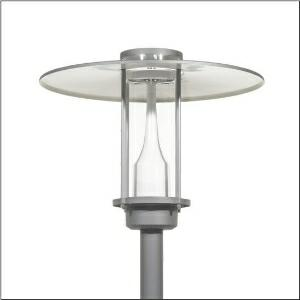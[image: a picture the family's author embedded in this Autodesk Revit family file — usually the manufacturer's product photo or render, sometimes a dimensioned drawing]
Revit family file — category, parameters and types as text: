
# Revit family: city-light_plus_iq___p1_0a_5xa5275ff14h_c9da
name_source: partatom
category: Lighting Fixtures
units: mm (PartAtom-declared; Revit-internal decimal feet)

## family parameters
Cut with Voids When Loaded = No
Host = Face
Light Source = No
Part Type = Normal
Room Calculation Point = No
Round Connector Dimension = Use Diameter
Shared = No

## types (1)
- --- (1 x LED, 1440 lm, 10.5 W, 3000K)
    Apparent Load = 11 VA
    CIE Flux Codes = 32 61 90 96 100
    Color Rendering = 70
    Color Temperature = 3000K
    Default Elevation = 1800 mm
    Description = City-Light Plus iQ, mast luminaire, Module 540 iQ-SR, primary light control with 3 zone facetted reflector, of plastic, silver coated, highly specular, structured, primary optical cover: cover, of PMMA, transparent, light distribution: P1.0a, light emission: direct distribution, primary light characteristic: strongly asymmetric, installation type: post-top, LED, High Power LED, rated luminous flux: 1.440lm, luminous efficacy: 137lm/W, light colour: 730, colour temperature: 3000K, control gear: iQ Street-Remote, control: Auto-Match, Temp-Guard, Lumen-Switch, Night-Set, Smart-Wire, Light-Fading, Desk-Remote (wireless, voltage-free reading and setting of iQ features in the workshop via application-optimized NFC function/RFID function), optimised constant luminous flux control (CLO 2.0), Street-Remote, pre-setting: logarithmic dimming characteristic, with terminal, 6-pole, max. 2.5mm², mains connection: 230..240V, AC, 50/60Hz, start of lifetime: 11W, end of service life: 11W, reduction: 5W, luminaire housing, upper part, of glass-fibre reinforced polyester, coated, Siteco® metallic grey (DB 702S), diameter: 750mm, height: 590mm, spigot size: d x l = 76 x 70mm (post-top) | with reducer (optional accessory) 60 x 70mm, mounting height: 3..5m, post-top mast mounting element, of diecast aluminium, coated, Siteco® metallic grey (DB 702S), Module 540 iQ-SR, traffic white (RAL 9016), equipment: standard, protection rating (complete): IP65, insulation class (complete): insulation class II (safety insulation), certification: CE, ENEC, VDE, packaging unit: 1 piece

Light Distribution: P1.0a
    Height = 590 mm
    Lamp = 1 x LED
    Lamp Light Flux = 1440 lm
    Lamp Power = 10.5 W
    Lamp count = 1
    Length = 750 mm
    Luminous efficacy = 137 lm/W
    Manufacturer = Siteco
    ModVariant = No
    Model = 5XA5275FF14H
    Number of Poles = 1
    OnlyDefault = Yes
    Power Factor = 1
    Product Name = City-Light Plus iQ | P1.0a
    Product group = mast luminaire | pylon top
    ProductGroupID = 6100
    Protection Class = Protection class II
    Protection Degree = IP 65
    RLX_Detail_Level = 1
    RLX_Emergency_Light_Flux = 0 lm
    RLX_Emergency_Type = 0
    RLX_Emergency_Type_DB = No
    RlxData = <blob elided: 60441 chars, md5=c65ad162>
    Socket = socket
    Standby Power = 0 W
    System Light Flux = 1440 lm
    System Power = 11 W
    Type Comments = factory setting: luminous flux: 100 % | dim-lin: 254 | 419 mA
    Type Image = l_1006456.jpg
    URL = http://relux.com
    VarID = @adj_160010
    Voltage = 0 V
    Weight = 0.00 kg
    Width = 0 mm  [stored 0 ft]

note: [stored X ft] marks values corroborated as IEEE doubles in the binary element streams (Revit-internal decimal feet)

## geometry (parser evidence)
native form markers: Blend x4, Sweep x12
no freeform markers — native parametric forms only
